# Revit family: xxShower_Base-American_Standard-60x32-A8002L_Series
name_source: partatom
category: Plumbing Fixtures
revit_build: Autodesk Revit 2014 (Build: 20130308_1515(x64)
units: mm (PartAtom-declared; Revit-internal decimal feet)

## types (2) — shared parameters
Assembly Code = D2010710
CW Connection = No
CWFU = 3
Clearance Between Studding = 0"
Default Elevation = 0"
Drain Length = 15 1/2"
Finish = Acrylic-American Standard-001-White
HW Connection = No
HWFU = 3
Height = 3 1/2"
Installation Type = Floor Mounted
Length = 32"
Manufacturer = American Standard
Material = Acrylic-American Standard-001-White
Price = Prices may vary. Please consult Manufacturer Representative for most up-to-date price list.
Strainer Finish = Stainless Steel-American Standard-Satin
URL = https://www.americanstandard-us.com
Vent Connection = No
WFU = 4
Warranty Information = Limited Lifetime Warranty
Waste Connection = Yes
Waste Connection Diameter = 3 1/4"
Waste Connection Radius = 1 5/8"
Width = 60"

## per-type parameters (varying)
| type | Description | Drain Location | Left Side Drain | Right Side Drain |
| A8002L.LHO | 60" x 32" Shower Base - Left Side Drain | 8" | Yes | No |
| A8002L.RHO | 60" x 32" Shower Base - Right Side Drain | 52" | No | Yes |

note: column(s) folded — value = type name in every type: Model

## geometry (parser evidence)
native form markers: Sweep x2
no freeform markers — native parametric forms only
